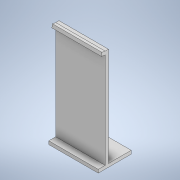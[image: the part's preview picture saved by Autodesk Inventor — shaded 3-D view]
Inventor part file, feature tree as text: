
AUTODESK INVENTOR PART (.ipt)
format: ipt  version: 2021 (Build 250183000, 183)  size: 128,512 bytes
history: native  units: mm
features: extrude x4, sketch x4, plane x1
ambient origin geometry x8: Origin, YZ Plane, XZ Plane, XY Plane, X Axis, Y Axis, Z Axis, Center Point
bodies: Solid1 (feature_tree)
feature tree (9):
  extrude  "Extrusion1"  Depth=20.0mm
  extrude  "Extrusion2"  Depth=2.0mm
  plane  "Work Plane9"
  extrude  "Extrusion6"  Depth=2.0mm
  extrude  "Extrusion7"  Depth=2.0mm TaperAngle=0.0deg
  sketch  "Sketch1"  dims[d0=30.0mm d1=20.0mm]
  sketch  "Sketch3"  dims[d2=2.0mm d3=0.0mm d5=2.0mm]
  sketch  "Sketch10"  dims[d6=62.0mm d7=0.0mm d26=2.0mm]
  sketch  "Sketch11"  dims[d27=2.0mm d28=0.0mm d29=2.0mm d30=0.0mm d16=0.5mm d17=0.872665mm d18=0.5mm d19=0.872665mm d23=0.5mm d24=0.872665mm d25=0.5mm]
